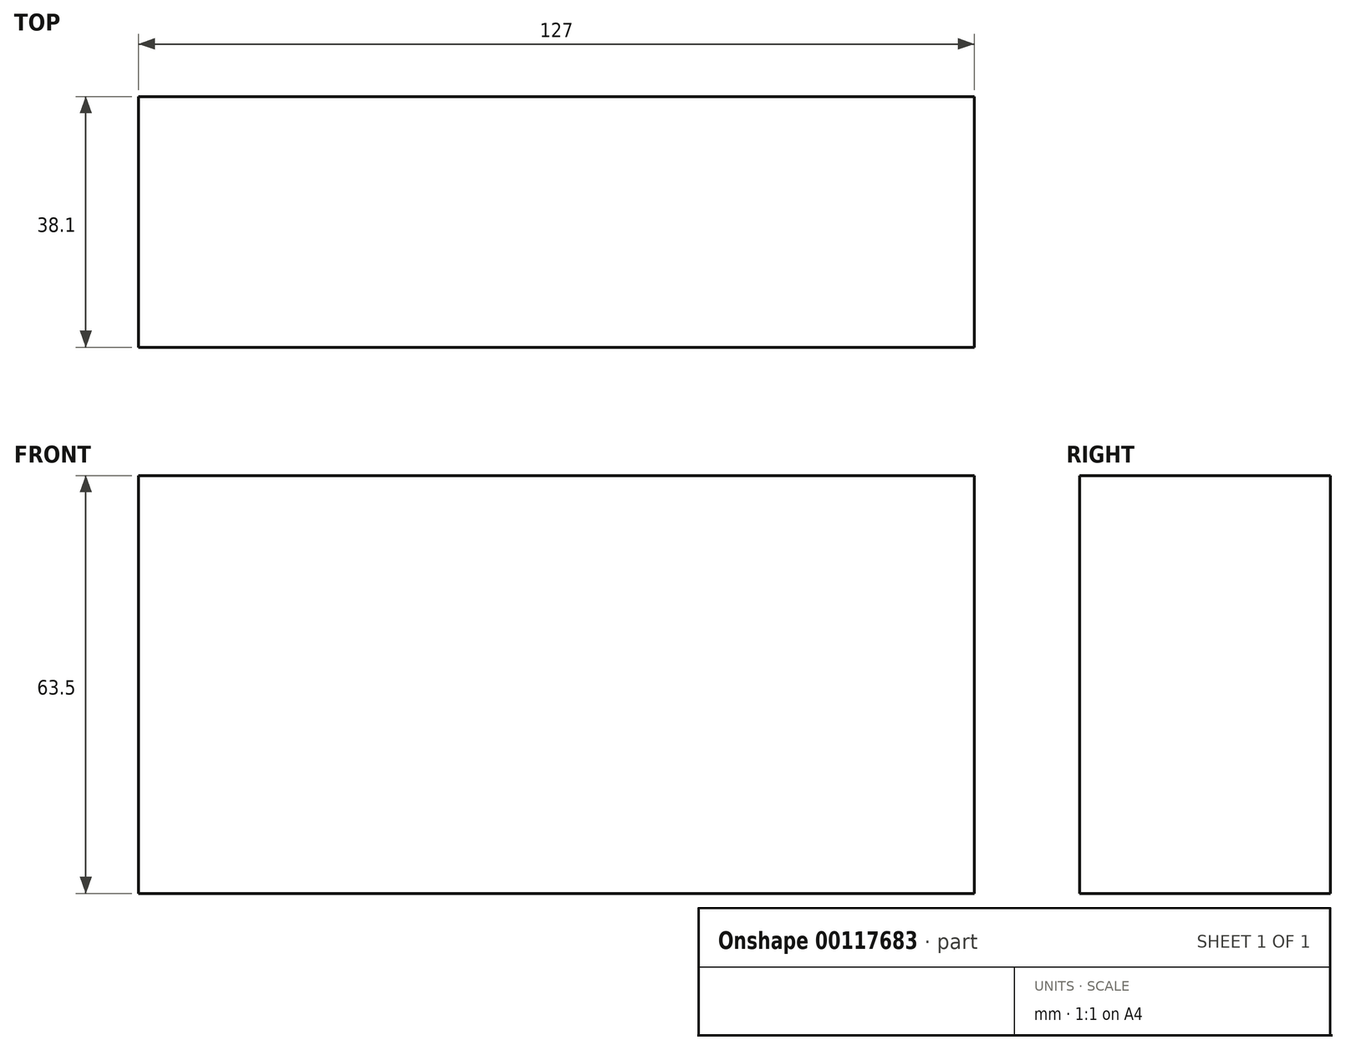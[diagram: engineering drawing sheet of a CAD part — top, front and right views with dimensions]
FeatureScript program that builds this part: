
annotation { "Feature Type Name" : "Feature", "Feature Type Description" : "" }
export const myFeature = defineFeature(function(context is Context, id is Id, definition is map)
    precondition{}
    {
        {
            var Q0;
            Q0=qCreatedBy(makeId("Front.planeOp"),FACE);
            var sketch = newSketch(context, id + "F0", { "sketchPlane" : qUnion([Q0])});
            skLineSegment(sketch, "E0.bottom", {"start": v(-72.3, 48.47) * mm, "end": v(54.7, 48.47) * mm});
            skLineSegment(sketch, "E0.top", {"start": v(-72.3, -15.03) * mm, "end": v(54.7, -15.03) * mm});
            skLineSegment(sketch, "E0.left", {"start": v(-72.3, 48.47) * mm, "end": v(-72.3, -15.03) * mm});
            skLineSegment(sketch, "E0.right", {"start": v(54.7, 48.47) * mm, "end": v(54.7, -15.03) * mm});
            skSolve(sketch);
        }
        {
            var Q0;
            Q0=makeQuery(id+"F0.imprint","IMPRINT",FACE,{"disambiguationData":[TD([[makeQuery(id+"F0.imprint","IMPRINT",EDGE,{"derivedFrom":sQuery(id+"F0.wireOp",EDGE,"E0.bottom")}),-1.0]])]});
            extrude(context, id + "F1", {"entities" : qUnion([Q0]), "depth" : 38.1 * mm});
        }
    });
